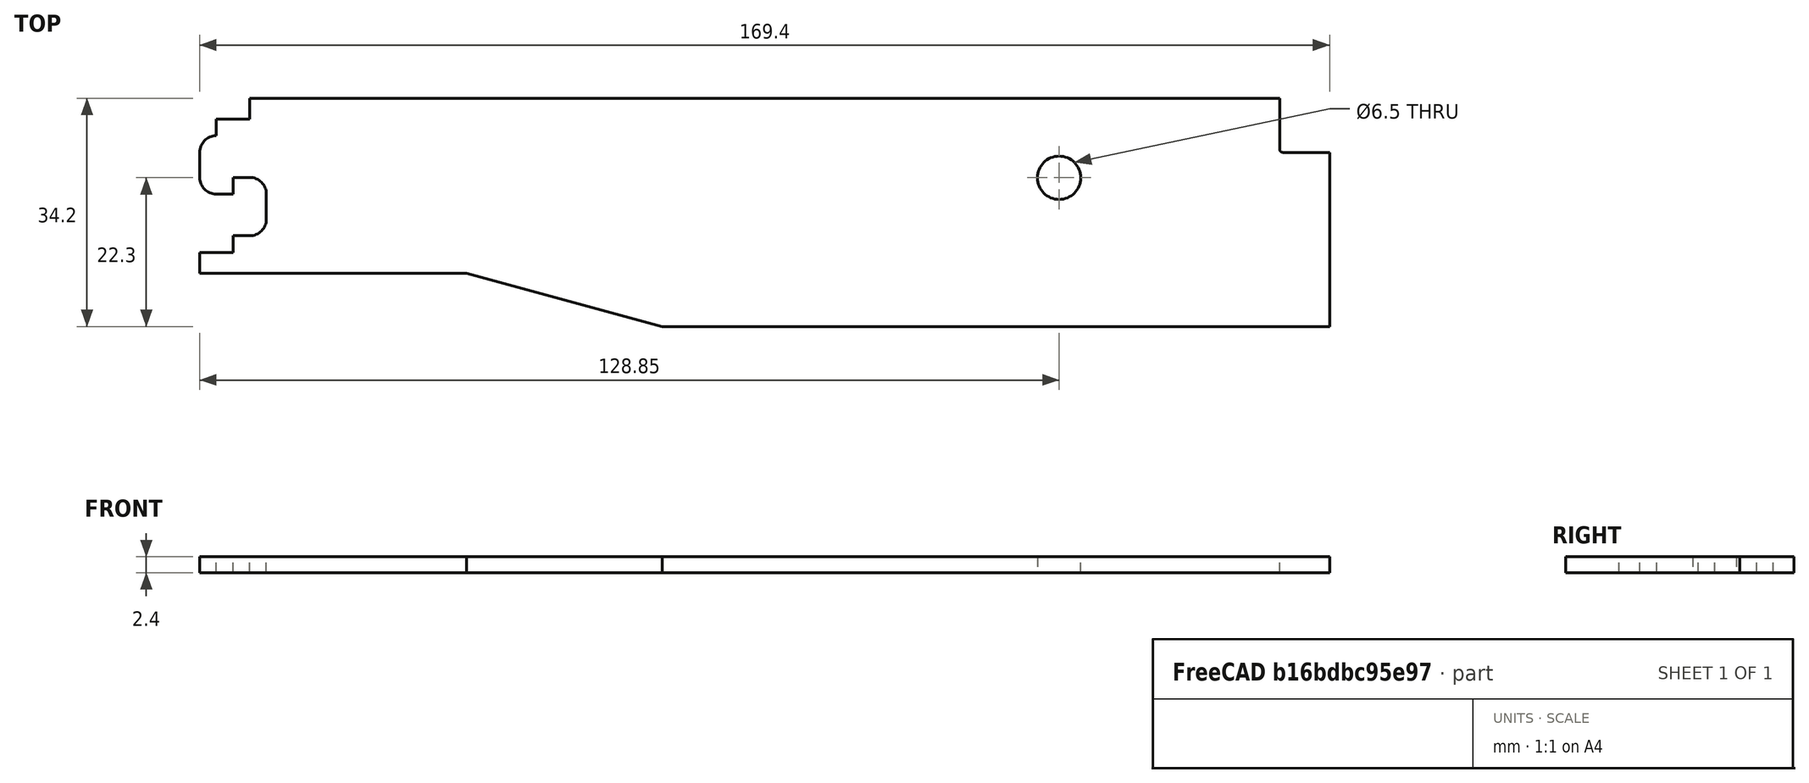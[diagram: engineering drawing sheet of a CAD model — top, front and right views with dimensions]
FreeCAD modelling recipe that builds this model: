
FCSTD DOCUMENT  (FreeCAD 0.19R0.19.2)
Label: v0_25
License: All rights reserved
LicenseURL: http://en.wikipedia.org/wiki/All_rights_reserved
objects: Sketcher::SketchObject×1, Part::Extrusion×1
note: 2 computed .brp shape members not serialized (recipe doc carries the construction recipe); baked Part::Feature solids carry a one-line shape summary decoded from their .brp

FEATURE [Sketcher::SketchObject] Sketch
  FullyConstrained = true
  sketch-geometry (25):
    g0: LineSegment StartX=0 StartY=0 StartZ=0 EndX=154.4 EndY=0 EndZ=0
    g1: Circle CenterX=121.35 CenterY=-11.9 CenterZ=0 NormalX=0 NormalY=0 NormalZ=1 AngleXU=0 Radius=3.25
    g2: LineSegment StartX=154.4 StartY=0 StartZ=0 EndX=154.4 EndY=-7.6 EndZ=0
    g3: ArcOfCircle CenterX=154.9 CenterY=-7.6 CenterZ=0 NormalX=0 NormalY=0 NormalZ=1 AngleXU=0 Radius=0.5 StartAngle=3.14159 EndAngle=4.71239
    g4: LineSegment StartX=-5 StartY=-3.1 StartZ=0 EndX=0 EndY=-3.1 EndZ=0
    g5: LineSegment StartX=-5 StartY=-3.1 StartZ=0 EndX=-5 EndY=-5.6 EndZ=0
    g6: LineSegment StartX=-7.5 StartY=-8.1 StartZ=0 EndX=-7.5 EndY=-11.85 EndZ=0
    g7: ArcOfCircle CenterX=-5 CenterY=-8.1 CenterZ=0 NormalX=0 NormalY=0 NormalZ=1 AngleXU=0 Radius=2.5 StartAngle=1.5708 EndAngle=3.14159
    g8: LineSegment StartX=-5 StartY=-14.35 StartZ=0 EndX=-2.5 EndY=-14.35 EndZ=0
    g9: ArcOfCircle CenterX=-5 CenterY=-11.85 CenterZ=0 NormalX=0 NormalY=0 NormalZ=1 AngleXU=0 Radius=2.5 StartAngle=3.14159 EndAngle=4.71239
    g10: LineSegment StartX=-2.5 StartY=-14.35 StartZ=0 EndX=-2.5 EndY=-11.85 EndZ=0
    g11: LineSegment StartX=-2.5 StartY=-11.85 StartZ=0 EndX=1.492e-13 EndY=-11.85 EndZ=0
    g12: ArcOfCircle CenterX=1.492e-13 CenterY=-14.35 CenterZ=0 NormalX=0 NormalY=0 NormalZ=1 AngleXU=0 Radius=2.5 StartAngle=8e-16 EndAngle=1.5708
    g13: LineSegment StartX=2.5 StartY=-14.35 StartZ=0 EndX=2.5 EndY=-18.1 EndZ=0
    g14: ArcOfCircle CenterX=1.474e-13 CenterY=-18.1 CenterZ=0 NormalX=0 NormalY=0 NormalZ=1 AngleXU=0 Radius=2.5 StartAngle=4.71239 EndAngle=6.28319
    g15: LineSegment StartX=-2.5 StartY=-20.6 StartZ=0 EndX=1.47e-13 EndY=-20.6 EndZ=0
    g16: LineSegment StartX=-2.5 StartY=-20.6 StartZ=0 EndX=-2.5 EndY=-23.1 EndZ=0
    g17: LineSegment StartX=-7.5 StartY=-23.1 StartZ=0 EndX=-2.5 EndY=-23.1 EndZ=0
    g18: LineSegment StartX=32.5209 StartY=-26.2 StartZ=0 EndX=-7.5 EndY=-26.2 EndZ=0
    g19: LineSegment StartX=61.85 StartY=-34.2 StartZ=0 EndX=161.9 EndY=-34.2 EndZ=0
    g20: LineSegment StartX=32.5209 StartY=-26.2 StartZ=0 EndX=61.85 EndY=-34.2 EndZ=0
    g21: LineSegment StartX=161.9 StartY=-8.1 StartZ=0 EndX=161.9 EndY=-34.2 EndZ=0
    g22: LineSegment StartX=154.9 StartY=-8.1 StartZ=0 EndX=161.9 EndY=-8.1 EndZ=0
    g23: LineSegment StartX=-7.5 StartY=-23.1 StartZ=0 EndX=-7.5 EndY=-26.2 EndZ=0
    g24: LineSegment StartX=0 StartY=0 StartZ=0 EndX=0 EndY=-3.1 EndZ=0
  constraints (60):
    c: PointOnObject(g0,g-2)
    c: Horizontal(g0)
    c: Distance(g0) = 154.4
    c: DistanceY(g-1,g0) = 0
    c: Block(g1)
    c: Vertical(g2)
    c: Distance(g2) = 7.6
    c: Coincident(g2,g0)
    c: Block(g3)
    c: Horizontal(g4)
    c: Vertical(g5)
    c: Coincident(g5,g4)
    c: Vertical(g6)
    c: Coincident(g7,g5)
    c: Block(g7)
    c: Coincident(g6,g7)
    c: Horizontal(g8)
    c: Coincident(g9,g6)
    c: Block(g9)
    c: Block(g8)
    c: Vertical(g10)
    c: Coincident(g10,g8)
    c: Horizontal(g11)
    c: Coincident(g11,g10)
    c: Coincident(g12,g11)
    c: Vertical(g13)
    c: Block(g12)
    c: Coincident(g13,g12)
    c: Coincident(g14,g13)
    c: Block(g14)
    c: Horizontal(g15)
    c: Coincident(g15,g14)
    c: Vertical(g16)
    c: Coincident(g16,g15)
    c: Horizontal(g17)
    c: Coincident(g17,g16)
    c: Block(g16)
    c: Block(g4)
    c: Horizontal(g19)
    c: Horizontal(g18)
    c: Block(g18)
    c: Block(g19)
    c: Coincident(g20,g18)
    c: Coincident(g20,g19)
    c: Vertical(g21)
    c: Distance(g21) = 26.1
    c: Coincident(g21,g19)
    c: Horizontal(g22)
    c: Coincident(g22,g21)
    c: Coincident(g22,g3)
    c: Distance(g22) = 7
    c: Distance(g16) = 2.5
    c: Distance(g16) = 2.5
    c: Block(g17)
    c: Vertical(g23)
    c: Coincident(g23,g17)
    c: Coincident(g23,g18)
    c: Vertical(g24)
    c: Coincident(g24,g0)
    c: Coincident(g24,g4)
FEATURE [Part::Extrusion] Extrude
  Base = -> Sketch
  Dir = (0,0,1)
  DirMode = 2
  FaceMakerClass = Part::FaceMakerBullseye
  LengthFwd = 2.4
  LengthRev = 0
  Solid = true
  Symmetric = false
